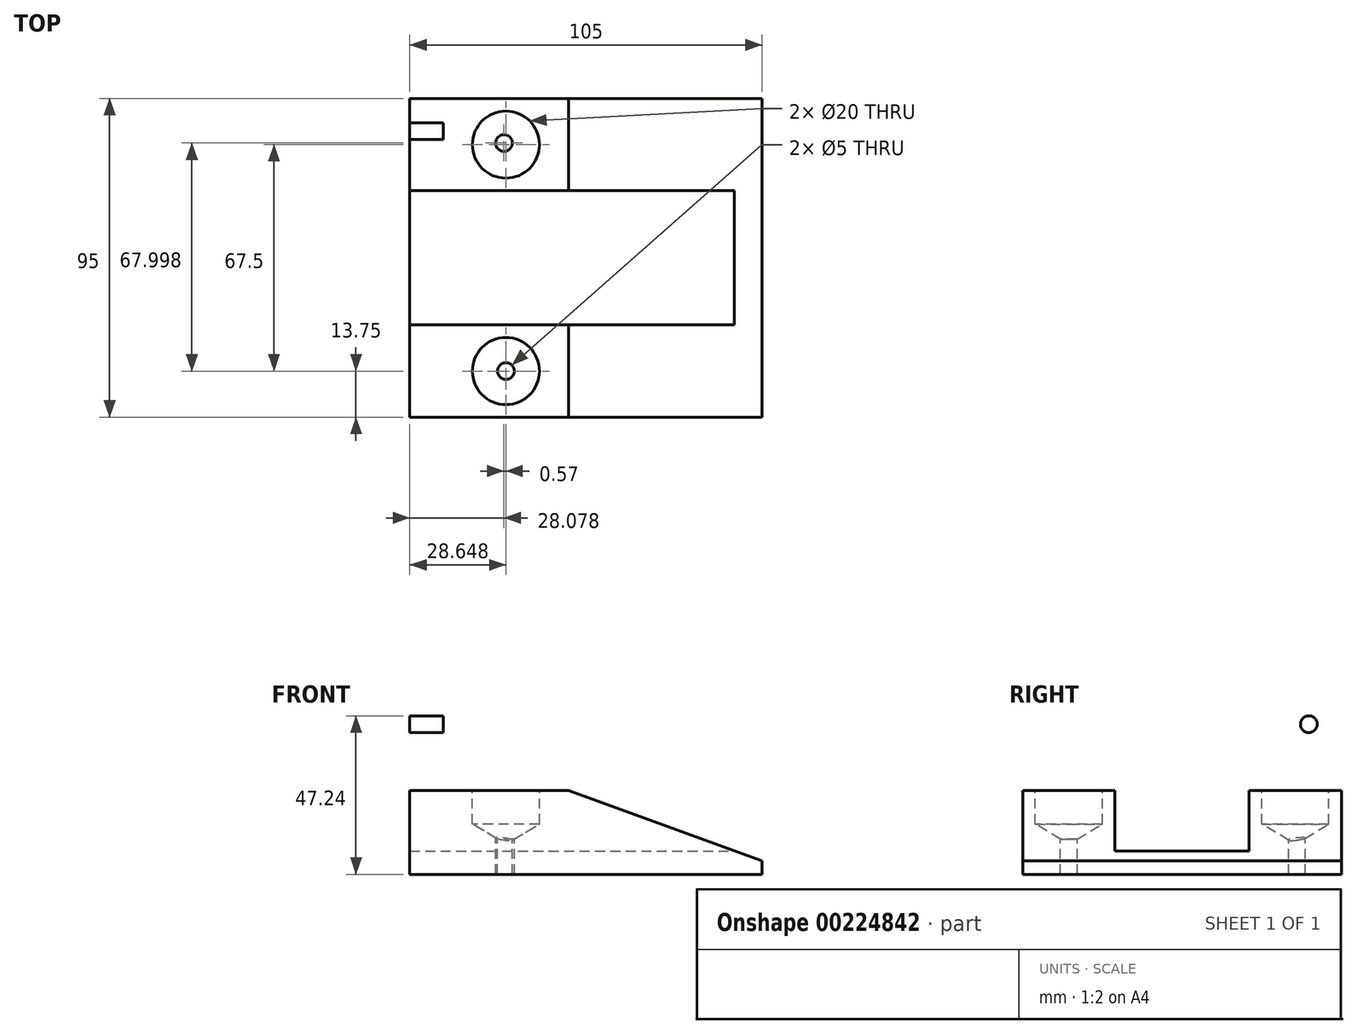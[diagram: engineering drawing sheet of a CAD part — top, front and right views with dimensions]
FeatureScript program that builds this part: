
annotation { "Feature Type Name" : "Feature", "Feature Type Description" : "" }
export const myFeature = defineFeature(function(context is Context, id is Id, definition is map)
    precondition{}
    {
        {
            var Q0;
            Q0=qCreatedBy(makeId("Front.planeOp"),FACE);
            var sketch = newSketch(context, id + "F0", { "sketchPlane" : qUnion([Q0])});
            skLineSegment(sketch, "E0.bottom", {"start": v(-47.3, -7.61) * mm, "end": v(-37.3, -7.61) * mm});
            skLineSegment(sketch, "E0.top", {"start": v(-47.3, -57.61) * mm, "end": v(-37.3, -57.61) * mm});
            skLineSegment(sketch, "E0.left", {"start": v(-47.3, -7.61) * mm, "end": v(-47.3, -57.61) * mm});
            skLineSegment(sketch, "E0.right", {"start": v(-37.3, -7.61) * mm, "end": v(-37.3, -57.61) * mm});
            skLineSegment(sketch, "E1", {"start": v(-37.3, -32.61) * mm, "end": v(0, -32.61) * mm});
            skLineSegment(sketch, "E2", {"start": v(0, -32.61) * mm, "end": v(57.7, -53.61) * mm});
            skLineSegment(sketch, "E3", {"start": v(57.7, -53.61) * mm, "end": v(57.7, -57.61) * mm});
            skLineSegment(sketch, "E4", {"start": v(57.7, -57.61) * mm, "end": v(-37.3, -57.61) * mm});
            skSolve(sketch);
        }
        {
            var Q0;
            Q0 = qSketchRegion(id + "F0", true);
            extrude(context, id + "F1", {"entities" : qUnion([Q0]), "depth" : 95 * mm, "symmetric" : true});
        }
        {
            var Q0;
            Q0=makeQuery(id+"F1.opExtrude","SWEPT_FACE",FACE,{"disambiguationData":[OSD([sQuery(id+"F0.wireOp",EDGE,"E1")])]});
            var sketch = newSketch(context, id + "F2", { "sketchPlane" : qUnion([Q0])});
            skLineSegment(sketch, "E5.bottom", {"start": v(-37.3, 20) * mm, "end": v(49.46, 20) * mm});
            skLineSegment(sketch, "E5.top", {"start": v(-37.3, -20) * mm, "end": v(49.46, -20) * mm});
            skLineSegment(sketch, "E5.left", {"start": v(-37.3, 20) * mm, "end": v(-37.3, -20) * mm});
            skLineSegment(sketch, "E5.right", {"start": v(49.46, 20) * mm, "end": v(49.46, -20) * mm});
            skSolve(sketch);
        }
        {
            var Q0;
            Q0 = qSketchRegion(id + "F2", true);
            extrude(context, id + "F3", {"entities" : qUnion([Q0]), "operationType" : NewBodyOperationType.REMOVE, "oppositeDirection" : true, "depth" : 18 * mm});
        }
        {
            var Q0;
            Q0=makeQuery(id+"F1.opExtrude","CAP_EDGE",EDGE,{"disambiguationData":[OSD([sQuery(id+"F0.wireOp",EDGE,"E0.bottom")])],"isStart":false});
            var Q1;
            Q1=makeQuery(id+"F1.opExtrude","CAP_EDGE",EDGE,{"disambiguationData":[OSD([sQuery(id+"F0.wireOp",EDGE,"E0.bottom")])],"isStart":true});
            fillet(context, id + "F4", {"entities" : qUnion([Q0, Q1]), "radius" : 10 * mm, "tangentPropagation" : true, "allowEdgeOverflow" : false});
        }
        {
            var Q0;
            Q0=makeQuery(id+"F3.boolean.opBoolean","MERGE",FACE,{"derivedFrom":[makeQuery(id+"F1.opExtrude","SWEPT_FACE",FACE,{"disambiguationData":[OSD([sQuery(id+"F0.wireOp",EDGE,"E0.right")])]}),makeQuery(id+"F3.opExtrude","SWEPT_FACE",FACE,{"disambiguationData":[OSD([sQuery(id+"F2.wireOp",EDGE,"E5.left")])]})]});
            var sketch = newSketch(context, id + "F5", { "sketchPlane" : qUnion([Q0])});
            skCircle(sketch, "E6", {"center": v(-37.78, -12.87) * mm, "radius": 2.5 * mm});
            skLineSegment(sketch, "E7", {"start": v(0, -7.61) * mm, "end": v(0, -50.61) * mm, "construction": true});
            skCircle(sketch, "E8.MirrorC", {"center": v(37.78, -12.87) * mm, "radius": 2.5 * mm});
            skSolve(sketch);
        }
        {
            var Q0;
            Q0=makeQuery(id+"F5.imprint","IMPRINT",FACE,{"disambiguationData":[TD([[makeQuery(id+"F5.imprint","IMPRINT",EDGE,{"derivedFrom":sQuery(id+"F5.wireOp",EDGE,"E6")}),1.0]])]});
            var Q1;
            Q1=makeQuery(id+"F5.imprint","IMPRINT",FACE,{"disambiguationData":[TD([[makeQuery(id+"F5.imprint","IMPRINT",EDGE,{"derivedFrom":sQuery(id+"F5.wireOp",EDGE,"E8.MirrorC")}),-1.0]])]});
            extrude(context, id + "F6", {"entities" : qUnion([Q0, Q1]), "operationType" : NewBodyOperationType.REMOVE, "endBound" : BoundingType.UP_TO_NEXT, "oppositeDirection" : true, "depth" : 25 * mm});
        }
        {
            var Q0;
            {var subQ2=sQuery(id+"F0.wireOp",EDGE,"E1");Q0=makeQuery(id+"F3.boolean.opBoolean","SPLIT",FACE,{"disambiguationData":[TD([makeQuery(id+"F3.opExtrude","SWEPT_FACE",FACE,{"disambiguationData":[OSD([sQuery(id+"F2.wireOp",EDGE,"E5.top")])]})])],"derivedFrom":makeQuery(id+"F1.opExtrude","SWEPT_FACE",FACE,{"disambiguationData":[OSD([subQ2])]})});}
            var sketch = newSketch(context, id + "F7", { "sketchPlane" : qUnion([Q0])});
            skCircle(sketch, "E9", {"center": v(-18.65, -33.75) * mm, "radius": 5 * mm});
            skPoint(sketch, "E9.centerSnap0", {"position": v(-37.3, -33.75) * mm});
            skPoint(sketch, "E9.centerSnap1", {"position": v(-18.65, -47.5) * mm});
            skSolve(sketch);
        }
        {
            var Q0;
            Q0=sQuery(id+"F7.wireOp",VERTEX,"E9.center");
            var Q1;
            Q1=makeQuery(id+"F1.opExtrude","SWEPT_BODY",BODY,{"disambiguationData":[OSD([sQuery(id+"F0.wireOp",EDGE,"E0.bottom"),sQuery(id+"F0.wireOp",EDGE,"E0.top"),sQuery(id+"F0.wireOp",EDGE,"E0.left"),sQuery(id+"F0.wireOp",EDGE,"E0.right"),sQuery(id+"F0.wireOp",EDGE,"E1"),sQuery(id+"F0.wireOp",EDGE,"E2"),sQuery(id+"F0.wireOp",EDGE,"E3"),sQuery(id+"F0.wireOp",EDGE,"E4")])]});
            hole(context, id + "F8", {"style" : HoleStyle.SIMPLE, "endStyle" : HoleEndStyle.BLIND, "holeDiameter" : 20 * mm, "holeDepth" : 10 * mm, "locations" : qUnion([Q0]), "scope" : qUnion([Q1])});
        }
        {
            var Q0;
            {var subQ2=sQuery(id+"F0.wireOp",EDGE,"E1");Q0=makeQuery(id+"F3.boolean.opBoolean","SPLIT",FACE,{"disambiguationData":[TD([makeQuery(id+"F3.opExtrude","SWEPT_FACE",FACE,{"disambiguationData":[OSD([sQuery(id+"F2.wireOp",EDGE,"E5.top")])]})])],"derivedFrom":makeQuery(id+"F1.opExtrude","SWEPT_FACE",FACE,{"disambiguationData":[OSD([subQ2])]})});}
            var sketch = newSketch(context, id + "F9", { "sketchPlane" : qUnion([Q0])});
            skCircle(sketch, "E10", {"center": v(-18.65, -33.75) * mm, "radius": 2.5 * mm});
            skSolve(sketch);
        }
        {
            var Q0;
            Q0=makeQuery(id+"F9.imprint","IMPRINT",FACE,{"disambiguationData":[TD([[makeQuery(id+"F9.imprint","IMPRINT",EDGE,{"derivedFrom":sQuery(id+"F9.wireOp",EDGE,"E10")}),1.0]])]});
            var Q1;
            Q1=sQuery(id+"F9.wireOp",EDGE,"E10");
            extrude(context, id + "F10", {"entities" : qUnion([Q0]), "operationType" : NewBodyOperationType.REMOVE, "surfaceEntities" : qUnion([Q1]), "oppositeDirection" : true, "depth" : 25 * mm});
        }
        {
            var Q0;
            {var subQ2=sQuery(id+"F0.wireOp",EDGE,"E1");Q0=makeQuery(id+"F3.boolean.opBoolean","SPLIT",FACE,{"disambiguationData":[TD([makeQuery(id+"F3.opExtrude","SWEPT_FACE",FACE,{"disambiguationData":[OSD([sQuery(id+"F2.wireOp",EDGE,"E5.bottom")])]})])],"derivedFrom":makeQuery(id+"F1.opExtrude","SWEPT_FACE",FACE,{"disambiguationData":[OSD([subQ2])]})});}
            var sketch = newSketch(context, id + "F11", { "sketchPlane" : qUnion([Q0])});
            skCircle(sketch, "E11", {"center": v(-18.65, 33.75) * mm, "radius": 5 * mm});
            skPoint(sketch, "E11.centerSnap0", {"position": v(-18.65, 20) * mm});
            skPoint(sketch, "E11.centerSnap1", {"position": v(-37.3, 33.75) * mm});
            skSolve(sketch);
        }
        {
            var Q0;
            Q0=sQuery(id+"F11.wireOp",VERTEX,"E11.center");
            var Q1;
            Q1=makeQuery(id+"F1.opExtrude","SWEPT_BODY",BODY,{"disambiguationData":[OSD([sQuery(id+"F0.wireOp",EDGE,"E0.bottom"),sQuery(id+"F0.wireOp",EDGE,"E0.top"),sQuery(id+"F0.wireOp",EDGE,"E0.left"),sQuery(id+"F0.wireOp",EDGE,"E0.right"),sQuery(id+"F0.wireOp",EDGE,"E1"),sQuery(id+"F0.wireOp",EDGE,"E2"),sQuery(id+"F0.wireOp",EDGE,"E3"),sQuery(id+"F0.wireOp",EDGE,"E4")])]});
            hole(context, id + "F12", {"style" : HoleStyle.SIMPLE, "endStyle" : HoleEndStyle.BLIND, "holeDiameter" : 20 * mm, "holeDepth" : 10 * mm, "locations" : qUnion([Q0]), "scope" : qUnion([Q1])});
        }
        {
            var Q0;
            {var subQ2=sQuery(id+"F0.wireOp",EDGE,"E1");Q0=makeQuery(id+"F3.boolean.opBoolean","SPLIT",FACE,{"disambiguationData":[TD([makeQuery(id+"F3.opExtrude","SWEPT_FACE",FACE,{"disambiguationData":[OSD([sQuery(id+"F2.wireOp",EDGE,"E5.bottom")])]})])],"derivedFrom":makeQuery(id+"F1.opExtrude","SWEPT_FACE",FACE,{"disambiguationData":[OSD([subQ2])]})});}
            var sketch = newSketch(context, id + "F13", { "sketchPlane" : qUnion([Q0])});
            skCircle(sketch, "E12", {"center": v(-19.22, 34.25) * mm, "radius": 2.5 * mm});
            skSolve(sketch);
        }
        {
            var Q0;
            Q0=makeQuery(id+"F13.imprint","IMPRINT",FACE,{"disambiguationData":[TD([[makeQuery(id+"F13.imprint","IMPRINT",EDGE,{"derivedFrom":sQuery(id+"F13.wireOp",EDGE,"E12")}),1.0]])]});
            extrude(context, id + "F14", {"entities" : qUnion([Q0]), "operationType" : NewBodyOperationType.REMOVE, "oppositeDirection" : true, "depth" : 25 * mm});
        }
    });
